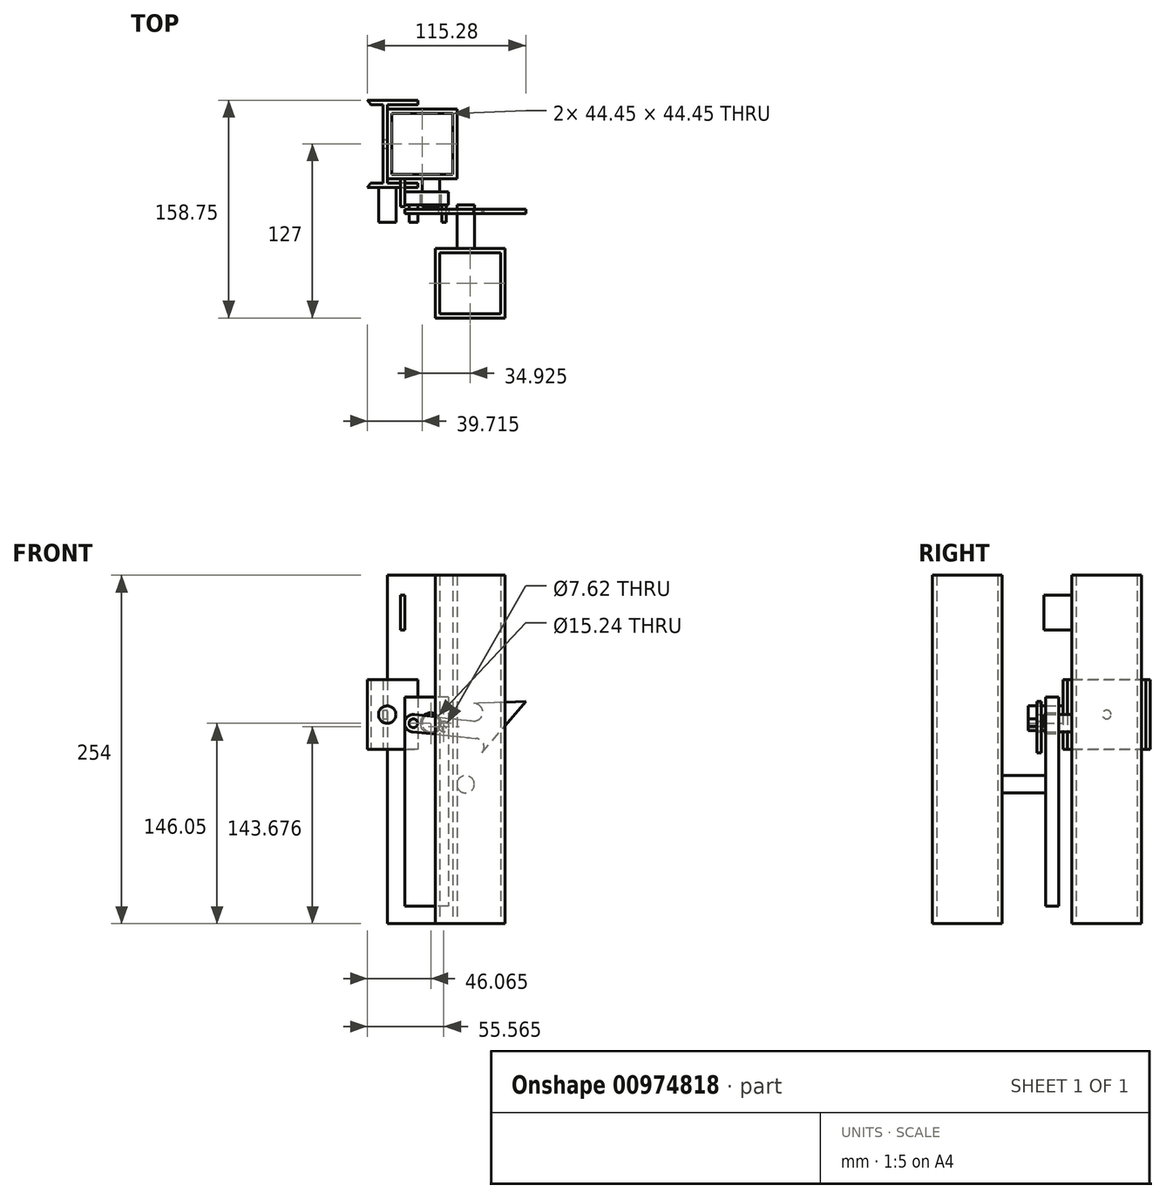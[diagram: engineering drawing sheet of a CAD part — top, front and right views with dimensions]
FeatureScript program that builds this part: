
annotation { "Feature Type Name" : "Feature", "Feature Type Description" : "" }
export const myFeature = defineFeature(function(context is Context, id is Id, definition is map)
    precondition{}
    {
        {
            var Q0;
            Q0=qCreatedBy(makeId("Top.planeOp"),FACE);
            var sketch = newSketch(context, id + "F0", { "sketchPlane" : qUnion([Q0])});
            skLineSegment(sketch, "E0", {"start": v(25.4, 31.75) * mm, "end": v(0, 31.75) * mm});
            skLineSegment(sketch, "E1", {"start": v(0, 31.75) * mm, "end": v(0, -31.75) * mm});
            skLineSegment(sketch, "E2", {"start": v(0, -31.75) * mm, "end": v(25.4, -31.75) * mm});
            skLineSegment(sketch, "E3", {"start": v(25.4, -31.75) * mm, "end": v(25.4, -28.57) * mm});
            skLineSegment(sketch, "E4", {"start": v(25.4, -28.57) * mm, "end": v(3.17, -28.57) * mm});
            skLineSegment(sketch, "E5", {"start": v(3.17, -28.57) * mm, "end": v(3.17, 28.57) * mm});
            skLineSegment(sketch, "E6", {"start": v(3.17, 28.57) * mm, "end": v(25.4, 28.57) * mm});
            skLineSegment(sketch, "E7", {"start": v(25.4, 28.57) * mm, "end": v(25.4, 31.75) * mm});
            skCircle(sketch, "E8", {"center": v(-50.8, 0) * mm, "radius": 50.8 * mm, "construction": true});
            skLineSegment(sketch, "E9", {"start": v(0, 28.57) * mm, "end": v(-8.8, 28.57) * mm});
            skLineSegment(sketch, "E10", {"start": v(0, 31.75) * mm, "end": v(-11.14, 31.75) * mm});
            skLineSegment(sketch, "E11", {"start": v(0, -28.57) * mm, "end": v(-8.8, -28.57) * mm});
            skLineSegment(sketch, "E12", {"start": v(0, -31.75) * mm, "end": v(-11.14, -31.75) * mm});
            skArc(sketch, "E13", {"start": v(-8.8, 28.57) * mm, "mid": v(-9.94, 30.19) * mm, "end": v(-11.14, 31.75) * mm});
            skArc(sketch, "E14", {"start": v(-11.14, -31.75) * mm, "mid": v(-9.94, -30.19) * mm, "end": v(-8.8, -28.57) * mm});
            skLineSegment(sketch, "E15", {"start": v(-100.23, -63.5) * mm, "end": v(128.61, -63.5) * mm, "construction": true});
            skLineSegment(sketch, "E16", {"start": v(-100.58, -69.85) * mm, "end": v(131.7, -69.85) * mm, "construction": true});
            skSolve(sketch);
        }
        {
            var Q0;
            {var subQ2=sQuery(id+"F0.wireOp",EDGE,"E9");Q0=makeQuery(id+"F0.imprint","IMPRINT",FACE,{"disambiguationData":[TD([[makeQuery(id+"F0.imprint","IMPRINT",EDGE,{"derivedFrom":subQ2}),-1.0]])]});}
            var Q1;
            {var subQ3=sQuery(id+"F0.wireOp",EDGE,"E0");Q1=makeQuery(id+"F0.imprint","IMPRINT",FACE,{"disambiguationData":[TD([[makeQuery(id+"F0.imprint","IMPRINT",EDGE,{"derivedFrom":subQ3}),1.0]])]});}
            var Q2;
            {var subQ2=sQuery(id+"F0.wireOp",EDGE,"E11");Q2=makeQuery(id+"F0.imprint","IMPRINT",FACE,{"disambiguationData":[TD([[makeQuery(id+"F0.imprint","IMPRINT",EDGE,{"derivedFrom":subQ2}),1.0]])]});}
            extrude(context, id + "F1", {"entities" : qUnion([Q0, Q1, Q2]), "depth" : 50.8 * mm, "offsetDistance" : 25.4 * mm});
        }
        {
            var Q0;
            Q0=makeQuery(id+"F1.opExtrude","SWEPT_FACE",FACE,{"disambiguationData":[OSD([sQuery(id+"F0.wireOp",EDGE,"E5")])]});
            var sketch = newSketch(context, id + "F2", { "sketchPlane" : qUnion([Q0])});
            skCircle(sketch, "E17", {"center": v(0, 25.4) * mm, "radius": 3.18 * mm});
            skSolve(sketch);
        }
        {
            var Q0;
            Q0=qSketchRegion(id+"F2",true);
            extrude(context, id + "F3", {"entities" : qUnion([Q0]), "operationType" : NewBodyOperationType.REMOVE, "endBound" : BoundingType.THROUGH_ALL, "oppositeDirection" : true, "depth" : 25.4 * mm, "offsetDistance" : 25.4 * mm});
        }
        {
            var Q0;
            Q0=qCreatedBy(makeId("Top.planeOp"),FACE);
            var sketch = newSketch(context, id + "F4", { "sketchPlane" : qUnion([Q0])});
            skCircle(sketch, "E18", {"center": v(-50.8, 0) * mm, "radius": 50.8 * mm});
            skCircle(sketch, "E19", {"center": v(-50.8, 0) * mm, "radius": 44.45 * mm});
            skLineSegment(sketch, "E20.bottom", {"start": v(3.17, 25.4) * mm, "end": v(53.97, 25.4) * mm});
            skLineSegment(sketch, "E20.top", {"start": v(3.18, -25.4) * mm, "end": v(53.98, -25.4) * mm});
            skLineSegment(sketch, "E20.left", {"start": v(3.17, 25.4) * mm, "end": v(3.18, -25.4) * mm});
            skLineSegment(sketch, "E20.right", {"start": v(53.97, 25.4) * mm, "end": v(53.98, -25.4) * mm});
            skLineSegment(sketch, "E21.bottom", {"start": v(6.35, 22.22) * mm, "end": v(50.8, 22.23) * mm});
            skLineSegment(sketch, "E21.top", {"start": v(6.35, -22.23) * mm, "end": v(50.8, -22.22) * mm});
            skLineSegment(sketch, "E21.left", {"start": v(6.35, 22.22) * mm, "end": v(6.35, -22.23) * mm});
            skLineSegment(sketch, "E21.right", {"start": v(50.8, 22.23) * mm, "end": v(50.8, -22.22) * mm});
            skLineSegment(sketch, "E22.bottom", {"start": v(38.1, -76.2) * mm, "end": v(88.9, -76.2) * mm});
            skLineSegment(sketch, "E22.top", {"start": v(38.1, -127) * mm, "end": v(88.9, -127) * mm});
            skLineSegment(sketch, "E22.left", {"start": v(38.1, -76.2) * mm, "end": v(38.1, -127) * mm});
            skLineSegment(sketch, "E22.right", {"start": v(88.9, -76.2) * mm, "end": v(88.9, -127) * mm});
            skLineSegment(sketch, "E23.bottom", {"start": v(41.28, -79.38) * mm, "end": v(85.73, -79.37) * mm});
            skLineSegment(sketch, "E23.top", {"start": v(41.28, -123.83) * mm, "end": v(85.72, -123.82) * mm});
            skLineSegment(sketch, "E23.left", {"start": v(41.28, -79.38) * mm, "end": v(41.28, -123.83) * mm});
            skLineSegment(sketch, "E23.right", {"start": v(85.73, -79.37) * mm, "end": v(85.73, -123.82) * mm});
            skSolve(sketch);
        }
        {
            var Q0;
            Q0=makeQuery(id+"F4.imprint","IMPRINT",FACE,{"disambiguationData":[TD([[makeQuery(id+"F4.imprint","IMPRINT",EDGE,{"derivedFrom":sQuery(id+"F4.wireOp",EDGE,"E20.bottom")}),-1.0]])]});
            var Q1;
            Q1=makeQuery(id+"F4.imprint","IMPRINT",FACE,{"disambiguationData":[TD([[makeQuery(id+"F4.imprint","IMPRINT",EDGE,{"derivedFrom":sQuery(id+"F4.wireOp",EDGE,"E22.bottom")}),-1.0]])]});
            extrude(context, id + "F5", {"entities" : qUnion([Q0, Q1]), "endBound" : BoundingType.SYMMETRIC, "depth" : 254 * mm, "offsetDistance" : 25.4 * mm});
        }
        {
            var Q0;
            Q0=makeQuery(id+"F1.opExtrude","SWEPT_FACE",FACE,{"disambiguationData":[OSD([sQuery(id+"F0.wireOp",EDGE,"E2"),sQuery(id+"F0.wireOp",EDGE,"E12")])]});
            var sketch = newSketch(context, id + "F6", { "sketchPlane" : qUnion([Q0])});
            skCircle(sketch, "E24", {"center": v(3.17, 25.4) * mm, "radius": 6.35 * mm});
            skSolve(sketch);
        }
        {
            var Q0;
            Q0=qSketchRegion(id+"F6",true);
            extrude(context, id + "F7", {"entities" : qUnion([Q0]), "operationType" : NewBodyOperationType.ADD, "depth" : 25.4 * mm, "offsetDistance" : 25.4 * mm});
        }
        {
            var Q0;
            Q0=makeQuery(id+"F5.opExtrude","SWEPT_FACE",FACE,{"disambiguationData":[OSD([sQuery(id+"F4.wireOp",EDGE,"E20.top")])]});
            var sketch = newSketch(context, id + "F8", { "sketchPlane" : qUnion([Q0])});
            skCircle(sketch, "E25", {"center": v(34.93, 19.05) * mm, "radius": 6.35 * mm});
            skLineSegment(sketch, "E26.bottom", {"start": v(47.63, 38.1) * mm, "end": v(15.88, 38.1) * mm});
            skLineSegment(sketch, "E26.top", {"start": v(47.63, -114.3) * mm, "end": v(15.88, -114.3) * mm});
            skLineSegment(sketch, "E26.left", {"start": v(47.63, 38.1) * mm, "end": v(47.63, -114.3) * mm});
            skLineSegment(sketch, "E26.right", {"start": v(15.88, 38.1) * mm, "end": v(15.88, -114.3) * mm});
            skCircle(sketch, "E27", {"center": v(34.93, 19.05) * mm, "radius": 7.62 * mm});
            skLineSegment(sketch, "E28.bottom", {"start": v(15.87, 112.34) * mm, "end": v(12.7, 112.34) * mm});
            skLineSegment(sketch, "E28.top", {"start": v(15.87, 86.94) * mm, "end": v(12.7, 86.94) * mm});
            skLineSegment(sketch, "E28.left", {"start": v(15.87, 112.34) * mm, "end": v(15.87, 86.94) * mm});
            skLineSegment(sketch, "E28.right", {"start": v(12.7, 112.34) * mm, "end": v(12.7, 86.94) * mm});
            skSolve(sketch);
        }
        {
            var Q0;
            Q0=makeQuery(id+"F8.imprint","IMPRINT",FACE,{"disambiguationData":[TD([[makeQuery(id+"F8.imprint","IMPRINT",EDGE,{"derivedFrom":sQuery(id+"F8.wireOp",EDGE,"E25")}),1.0]])]});
            var Q1;
            Q1=makeQuery(id+"F8.imprint","IMPRINT",FACE,{"disambiguationData":[TD([[makeQuery(id+"F8.imprint","IMPRINT",EDGE,{"derivedFrom":sQuery(id+"F8.wireOp",EDGE,"E28.bottom")}),1.0]])]});
            extrude(context, id + "F9", {"entities" : qUnion([Q0, Q1]), "operationType" : NewBodyOperationType.ADD, "depth" : 20.32 * mm, "offsetDistance" : 25.4 * mm});
        }
        {
            var Q0;
            Q0=makeQuery(id+"F1.opExtrude","SWEPT_FACE",FACE,{"disambiguationData":[OSD([sQuery(id+"F0.wireOp",EDGE,"E2"),sQuery(id+"F0.wireOp",EDGE,"E12")])]});
            var sketch = newSketch(context, id + "F10", { "sketchPlane" : qUnion([Q0])});
            skCircle(sketch, "E29", {"center": v(66.46, 27.09) * mm, "radius": 6.35 * mm, "construction": true});
            skCircle(sketch, "E30", {"center": v(22.23, 19.05) * mm, "radius": 3.18 * mm});
            skCircle(sketch, "E31.MirrorC", {"center": v(67.42, 1.7) * mm, "radius": 6.35 * mm, "construction": true});
            skCircle(sketch, "E32", {"center": v(34.92, 19.05) * mm, "radius": 6.35 * mm, "construction": true});
            skLineSegment(sketch, "E33", {"start": v(-15.47, 17.62) * mm, "end": v(114.37, 22.56) * mm, "construction": true});
            skLineSegment(sketch, "E34", {"start": v(22.9, 25.37) * mm, "end": v(65.78, 20.78) * mm});
            skLineSegment(sketch, "E35", {"start": v(68.03, -14.3) * mm, "end": v(65.53, 51.44) * mm, "construction": true});
            skArc(sketch, "E36", {"start": v(65.78, 20.78) * mm, "mid": v(72.8, 26.87) * mm, "end": v(66.22, 33.43) * mm});
            skLineSegment(sketch, "E37", {"start": v(72.25, -2.42) * mm, "end": v(104.14, 34.88) * mm});
            skLineSegment(sketch, "E38", {"start": v(104.14, 34.88) * mm, "end": v(66.22, 33.43) * mm});
            skLineSegment(sketch, "E39", {"start": v(21.58, 12.74) * mm, "end": v(68.06, 8.02) * mm});
            skArc(sketch, "E40", {"start": v(68.06, 8.02) * mm, "mid": v(73.32, 4.07) * mm, "end": v(72.25, -2.42) * mm});
            skCircle(sketch, "E41", {"center": v(22.23, 19.05) * mm, "radius": 6.35 * mm});
            skLineSegment(sketch, "E42", {"start": v(-18.7, 23.44) * mm, "end": v(111.81, 9.46) * mm, "construction": true});
            skLineSegment(sketch, "E43", {"start": v(68.46, 45.75) * mm, "end": v(61.72, -17.14) * mm, "construction": true});
            skCircle(sketch, "E44", {"center": v(44.43, 16.68) * mm, "radius": 3.81 * mm});
            skSolve(sketch);
        }
        {
            var Q0;
            {var subQ0=sQuery(id+"F10.wireOp",EDGE,"E36");Q0=makeQuery(id+"F10.imprint","IMPRINT",FACE,{"disambiguationData":[TD([[makeQuery(id+"F10.imprint","IMPRINT",EDGE,{"derivedFrom":subQ0}),-1.0]])]});}
            var Q1;
            {var subQ0=sQuery(id+"F10.wireOp",EDGE,"E41");var subQ1=makeQuery(id+"F1.opExtrude","SWEPT_EDGE",EDGE,{"disambiguationData":[OSD([sQuery(id+"F0.wireOp",EDGE,"E2"),sQuery(id+"F0.wireOp",EDGE,"E3")])]});var subQ2=makeQuery(id+"F10.imprint","INTERSECT",VERTEX,{"disambiguationData":[OD(0.0)],"derivedFrom":[subQ1,subQ0]});Q1=makeQuery(id+"F10.imprint","IMPRINT",FACE,{"disambiguationData":[TD([[makeQuery(id+"F10.imprint","IMPRINT",EDGE,{"disambiguationData":[TD([[subQ2,1.0]])],"derivedFrom":subQ0}),1.0]])]});}
            var Q2;
            {var subQ5=sQuery(id+"F10.wireOp",EDGE,"E30");Q2=makeQuery(id+"F10.imprint","IMPRINT",FACE,{"disambiguationData":[TD([[makeQuery(id+"F10.imprint","IMPRINT",EDGE,{"derivedFrom":subQ5}),-1.0]])]});}
            var Q3;
            {var subQ0=sQuery(id+"F10.wireOp",EDGE,"E41");var subQ1=sQuery(id+"F10.wireOp",EDGE,"E34");var subQ2=makeQuery(id+"F10.imprint","INTERSECT",VERTEX,{"derivedFrom":[subQ1,subQ0]});Q3=makeQuery(id+"F10.imprint","IMPRINT",FACE,{"disambiguationData":[TD([[makeQuery(id+"F10.imprint","IMPRINT",EDGE,{"disambiguationData":[TD([[subQ2,-1.0]])],"derivedFrom":subQ1}),-1.0]])]});}
            var Q4;
            {var subQ0=sQuery(id+"F10.wireOp",EDGE,"E41");var subQ1=sQuery(id+"F10.wireOp",EDGE,"E39");var subQ2=makeQuery(id+"F10.imprint","INTERSECT",VERTEX,{"derivedFrom":[subQ1,subQ0]});Q4=makeQuery(id+"F10.imprint","IMPRINT",FACE,{"disambiguationData":[TD([[makeQuery(id+"F10.imprint","IMPRINT",EDGE,{"disambiguationData":[TD([[subQ2,-1.0]])],"derivedFrom":subQ1}),1.0]])]});}
            extrude(context, id + "F11", {"entities" : qUnion([Q0, Q1, Q2, Q3, Q4]), "depth" : 19.05 * mm, "offsetDistance" : 25.4 * mm, "hasSecondDirection" : true, "secondDirectionOppositeDirection" : false, "secondDirectionDepth" : 15.88 * mm});
        }
        {
            var Q0;
            Q0=makeQuery(id+"F8.imprint","IMPRINT",FACE,{"disambiguationData":[TD([[makeQuery(id+"F8.imprint","IMPRINT",EDGE,{"derivedFrom":sQuery(id+"F8.wireOp",EDGE,"E26.bottom")}),1.0]])]});
            var Q1;
            {var subQ7=sQuery(id+"F8.wireOp",EDGE,"E26.top");Q1=makeQuery(id+"F8.imprint","IMPRINT",FACE,{"disambiguationData":[TD([[makeQuery(id+"F8.imprint","IMPRINT",EDGE,{"derivedFrom":subQ7}),-1.0]])]});}
            extrude(context, id + "F12", {"entities" : qUnion([Q0, Q1]), "depth" : 19.05 * mm, "offsetDistance" : 25.4 * mm, "hasSecondDirection" : true, "secondDirectionOppositeDirection" : false, "secondDirectionDepth" : 9.52 * mm});
        }
        {
            var Q0;
            Q0=makeQuery(id+"F12.opExtrude","CAP_FACE",FACE,{"disambiguationData":[OSD([sQuery(id+"F8.wireOp",EDGE,"E26.bottom"),sQuery(id+"F8.wireOp",EDGE,"E26.top"),sQuery(id+"F8.wireOp",EDGE,"E26.left"),sQuery(id+"F8.wireOp",EDGE,"E26.right"),sQuery(id+"F8.wireOp",EDGE,"E27")])],"isStart":false});
            var sketch = newSketch(context, id + "F13", { "sketchPlane" : qUnion([Q0])});
            skCircle(sketch, "E45", {"center": v(22.23, 19.05) * mm, "radius": 3.18 * mm});
            skCircle(sketch, "E46", {"center": v(44.68, 15.24) * mm, "radius": 1.59 * mm});
            skSolve(sketch);
        }
        {
            var Q0;
            Q0=makeQuery(id+"F13.imprint","IMPRINT",FACE,{"disambiguationData":[TD([[makeQuery(id+"F13.imprint","IMPRINT",EDGE,{"derivedFrom":sQuery(id+"F13.wireOp",EDGE,"E45")}),1.0]])]});
            var Q1;
            Q1=makeQuery(id+"F13.imprint","IMPRINT",FACE,{"disambiguationData":[TD([[makeQuery(id+"F13.imprint","IMPRINT",EDGE,{"derivedFrom":sQuery(id+"F13.wireOp",EDGE,"E46")}),1.0]])]});
            var Q2;
            Q2=makeQuery(id+"F13.imprint","IMPRINT",FACE,{"disambiguationData":[TD([[makeQuery(id+"F13.imprint","IMPRINT",EDGE,{"derivedFrom":sQuery(id+"F13.wireOp",EDGE,"uAvvqMaT-fYfl-bLKJ-mTmU-EZ5cuX3X6mni")}),1.0]])]});
            extrude(context, id + "F14", {"entities" : qUnion([Q0, Q1, Q2]), "operationType" : NewBodyOperationType.ADD, "depth" : 12.7 * mm, "offsetDistance" : 25.4 * mm});
        }
        {
            var Q0;
            Q0=makeQuery(id+"F5.opExtrude","SWEPT_FACE",FACE,{"disambiguationData":[OSD([sQuery(id+"F4.wireOp",EDGE,"E22.bottom")])]});
            var sketch = newSketch(context, id + "F15", { "sketchPlane" : qUnion([Q0])});
            skCircle(sketch, "E47", {"center": v(-60.32, -25.4) * mm, "radius": 6.35 * mm});
            skSolve(sketch);
        }
        {
            var Q0;
            Q0 = qSketchRegion(id + "F15", true);
            extrude(context, id + "F16", {"entities" : qUnion([Q0]), "operationType" : NewBodyOperationType.ADD, "depth" : 31.75 * mm, "offsetDistance" : 25.4 * mm});
        }
    });
